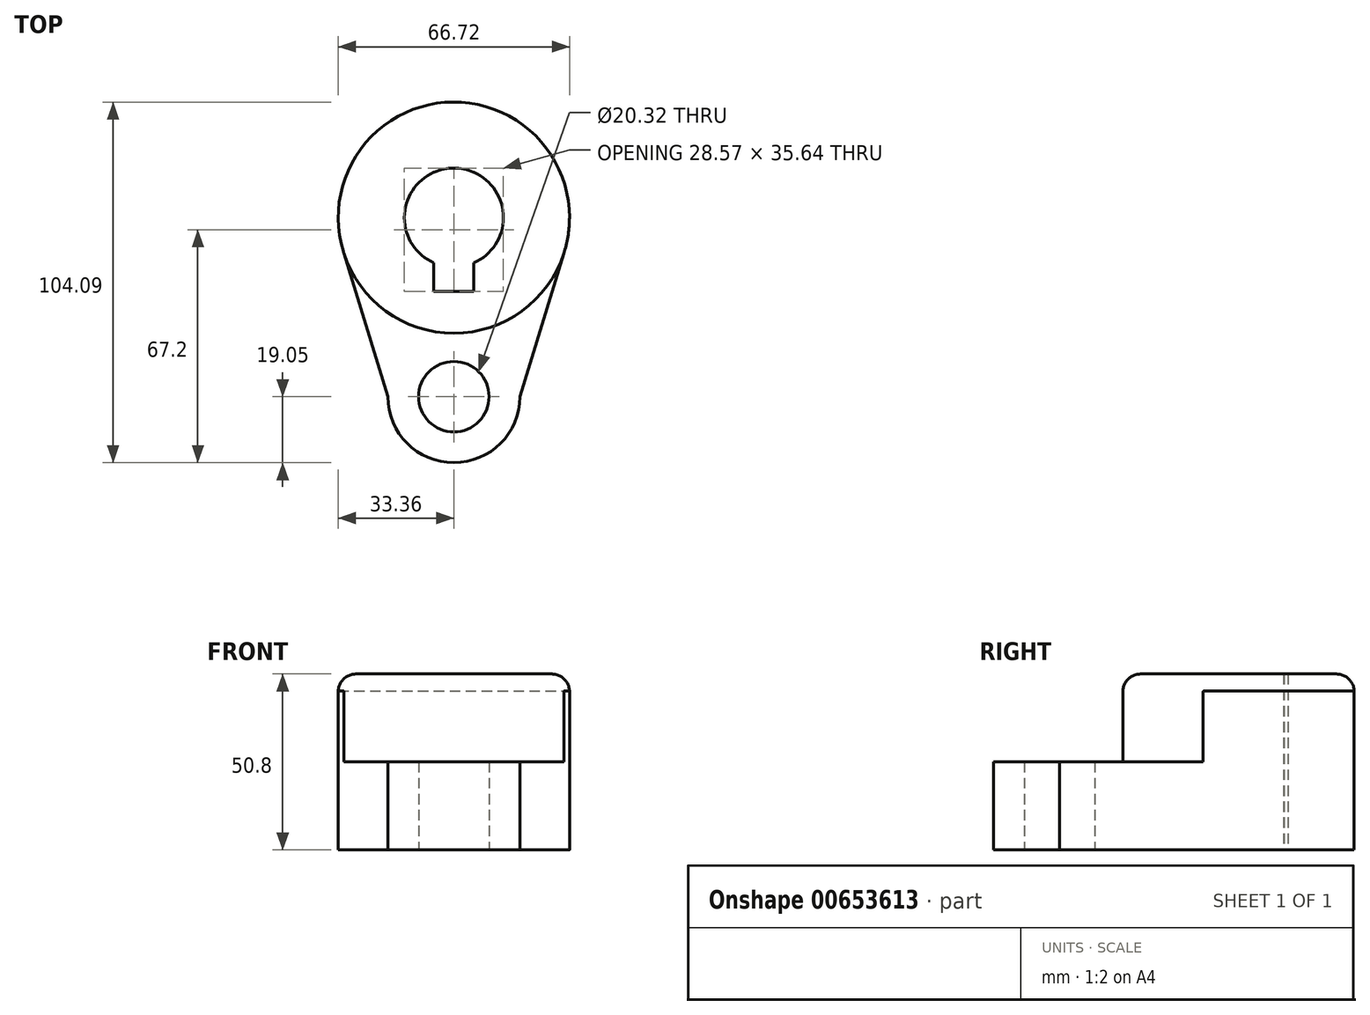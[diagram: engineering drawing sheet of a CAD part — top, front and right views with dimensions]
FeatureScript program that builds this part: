
annotation { "Feature Type Name" : "Feature", "Feature Type Description" : "" }
export const myFeature = defineFeature(function(context is Context, id is Id, definition is map)
    precondition{}
    {
        {
            var Q0;
            Q0=qCreatedBy(makeId("Top.planeOp"),FACE);
            var sketch = newSketch(context, id + "F0", { "sketchPlane" : qUnion([Q0])});
            skCircle(sketch, "E0", {"center": v(0, 51.68) * mm, "radius": 33.36 * mm});
            skArc(sketch, "E1", {"start": v(5.8, 38.62) * mm, "mid": v(0, 65.97) * mm, "end": v(-5.8, 38.62) * mm});
            skCircle(sketch, "E2", {"center": v(0, 0) * mm, "radius": 10.16 * mm});
            skLineSegment(sketch, "E3", {"start": v(-19.05, 0) * mm, "end": v(-31.9, 41.9) * mm});
            skLineSegment(sketch, "E4", {"start": v(31.9, 41.9) * mm, "end": v(19.05, 0) * mm});
            skArc(sketch, "E5", {"start": v(-19.05, 0) * mm, "mid": v(0, -19.05) * mm, "end": v(19.05, 0) * mm});
            skLineSegment(sketch, "E6.bottom", {"start": v(5.8, 30.33) * mm, "end": v(-5.8, 30.33) * mm});
            skLineSegment(sketch, "E6.top", {"start": v(5.8, 64.8) * mm, "end": v(5.67, 64.8) * mm});
            skLineSegment(sketch, "E6.left", {"start": v(5.8, 30.33) * mm, "end": v(5.8, 38.62) * mm});
            skLineSegment(sketch, "E6.right", {"start": v(-5.8, 30.33) * mm, "end": v(-5.8, 38.62) * mm});
            skPoint(sketch, "E6.middle", {"position": v(0, 47.56) * mm});
            skLineSegment(sketch, "E7.trimOffspring", {"start": v(-5.8, 64.74) * mm, "end": v(-5.8, 64.8) * mm});
            skLineSegment(sketch, "E8.trimOffspring", {"start": v(5.8, 64.74) * mm, "end": v(5.8, 64.8) * mm});
            skLineSegment(sketch, "E9.trimOffspring", {"start": v(-5.67, 64.8) * mm, "end": v(-5.8, 64.8) * mm});
            skSolve(sketch);
        }
        {
            var Q0;
            Q0=makeQuery(id+"F0.imprint","IMPRINT",FACE,{"disambiguationData":[TD([[makeQuery(id+"F0.imprint","IMPRINT",EDGE,{"derivedFrom":sQuery(id+"F0.wireOp",EDGE,"E2")}),-1.0]])]});
            var Q1;
            Q1=makeQuery(id+"F0.imprint","IMPRINT",FACE,{"disambiguationData":[TD([[makeQuery(id+"F0.imprint","IMPRINT",EDGE,{"derivedFrom":sQuery(id+"F0.wireOp",EDGE,"E6.bottom")}),1.0]])]});
            extrude(context, id + "F1", {"entities" : qUnion([Q0, Q1]), "depth" : 25.4 * mm, "offsetDistance" : 25.4 * mm});
        }
        {
            var Q0;
            Q0=makeQuery(id+"F1.opExtrude","CAP_FACE",FACE,{"disambiguationData":[OSD([sQuery(id+"F0.wireOp",EDGE,"E0"),sQuery(id+"F0.wireOp",EDGE,"E1"),sQuery(id+"F0.wireOp",EDGE,"E2"),sQuery(id+"F0.wireOp",EDGE,"E3"),sQuery(id+"F0.wireOp",EDGE,"E4"),sQuery(id+"F0.wireOp",EDGE,"E5"),sQuery(id+"F0.wireOp",EDGE,"E6.bottom"),sQuery(id+"F0.wireOp",EDGE,"E6.top"),sQuery(id+"F0.wireOp",EDGE,"E6.left"),sQuery(id+"F0.wireOp",EDGE,"E6.right"),sQuery(id+"F0.wireOp",EDGE,"E7.trimOffspring"),sQuery(id+"F0.wireOp",EDGE,"E8.trimOffspring"),sQuery(id+"F0.wireOp",EDGE,"E9.trimOffspring")])],"isStart":false});
            var sketch = newSketch(context, id + "F2", { "sketchPlane" : qUnion([Q0])});
            skCircle(sketch, "E10", {"center": v(0, 51.68) * mm, "radius": 33.37 * mm});
            skArc(sketch, "E11", {"start": v(5.78, 38.62) * mm, "mid": v(0, 65.96) * mm, "end": v(-5.78, 38.62) * mm});
            skLineSegment(sketch, "E12.top", {"start": v(5.78, 30.44) * mm, "end": v(-5.78, 30.44) * mm});
            skLineSegment(sketch, "E12.left", {"start": v(5.78, 38.62) * mm, "end": v(5.78, 30.44) * mm});
            skLineSegment(sketch, "E12.right", {"start": v(-5.78, 38.62) * mm, "end": v(-5.78, 30.44) * mm});
            skPoint(sketch, "E12.middle", {"position": v(0, 44.14) * mm});
            skPoint(sketch, "E12.bottom.end.orphan", {"position": v(-5.78, 57.84) * mm});
            skPoint(sketch, "E12.bottom.start.orphan", {"position": v(5.78, 57.84) * mm});
            skSolve(sketch);
        }
        {
            var Q0;
            {var subQ10=makeQuery(id+"F1.opExtrude","CAP_EDGE",EDGE,{"disambiguationData":[OSD([sQuery(id+"F0.wireOp",EDGE,"E0")])],"isStart":false});Q0=makeQuery(id+"F2.imprint","IMPRINT",FACE,{"disambiguationData":[TD([[makeQuery(id+"F2.imprint","IMPRINT",EDGE,{"derivedFrom":subQ10}),1.0]])]});}
            extrude(context, id + "F3", {"entities" : qUnion([Q0]), "operationType" : NewBodyOperationType.ADD, "depth" : 25.4 * mm, "offsetDistance" : 25.4 * mm});
        }
        {
            var Q0;
            Q0=makeQuery(id+"F3.opExtrude","CAP_EDGE",EDGE,{"disambiguationData":[OSD([sQuery(id+"F2.wireOp",EDGE,"E10")])],"isStart":false});
            fillet(context, id + "F4", {"entities" : qUnion([Q0]), "radius" : 5.08 * mm, "tangentPropagation" : true, "allowEdgeOverflow" : false});
        }
    });
